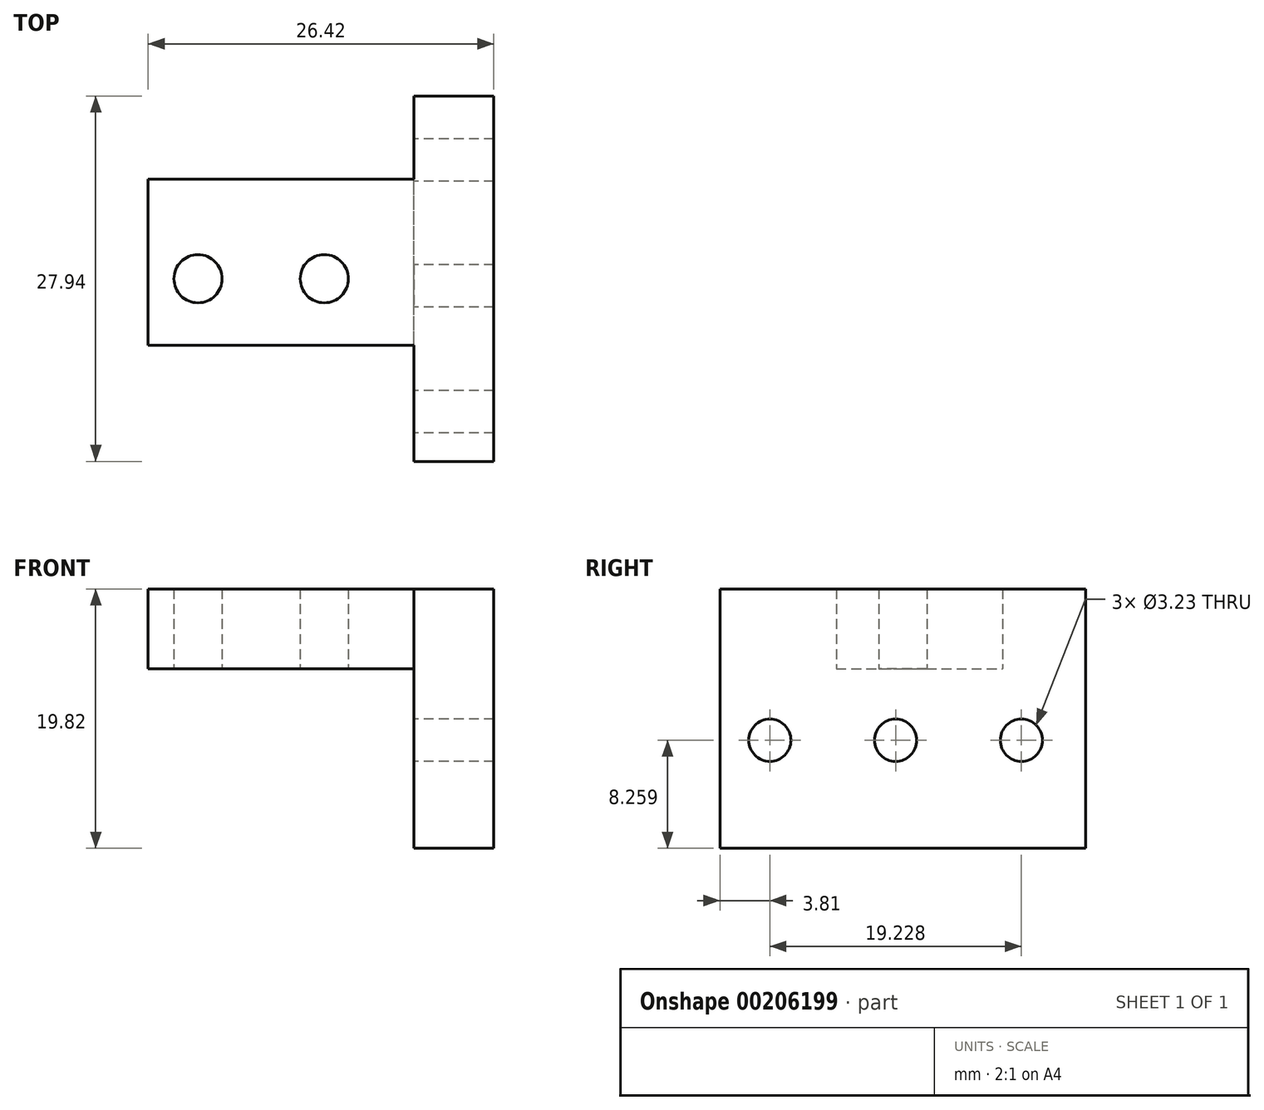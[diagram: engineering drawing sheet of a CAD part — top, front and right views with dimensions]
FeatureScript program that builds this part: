
annotation { "Feature Type Name" : "Feature", "Feature Type Description" : "" }
export const myFeature = defineFeature(function(context is Context, id is Id, definition is map)
    precondition{}
    {
        {
            var Q0;
            Q0=qCreatedBy(makeId("Top.planeOp"),FACE);
            var sketch = newSketch(context, id + "F0", { "sketchPlane" : qUnion([Q0])});
            skLineSegment(sketch, "E0.bottom", {"start": v(0, 0) * mm, "end": v(20.32, 0) * mm});
            skLineSegment(sketch, "E0.top", {"start": v(0, 12.7) * mm, "end": v(20.32, 12.7) * mm});
            skLineSegment(sketch, "E0.left", {"start": v(0, 0) * mm, "end": v(0, 12.7) * mm});
            skLineSegment(sketch, "E0.right", {"start": v(20.32, 0) * mm, "end": v(20.32, 12.7) * mm});
            skCircle(sketch, "E1", {"center": v(3.8, 5.08) * mm, "radius": 1.84 * mm});
            skCircle(sketch, "E2.1.0.0", {"center": v(13.46, 5.08) * mm, "radius": 1.84 * mm});
            skLineSegment(sketch, "E2.direction1", {"start": v(3.8, 5.08) * mm, "end": v(13.46, 5.08) * mm, "construction": true});
            skSolve(sketch);
        }
        {
            var Q0;
            Q0 = qSketchRegion(id + "F0", true);
            extrude(context, id + "F1", {"entities" : qUnion([Q0]), "depth" : 6.1 * mm});
        }
        {
            var Q0;
            Q0=makeQuery(id+"F1.opExtrude","CAP_FACE",FACE,{"disambiguationData":[OSD([sQuery(id+"F0.wireOp",EDGE,"E0.bottom"),sQuery(id+"F0.wireOp",EDGE,"E0.top"),sQuery(id+"F0.wireOp",EDGE,"E0.left"),sQuery(id+"F0.wireOp",EDGE,"E0.right"),sQuery(id+"F0.wireOp",EDGE,"E1"),sQuery(id+"F0.wireOp",EDGE,"E2.1.0.0")])],"isStart":false});
            var sketch = newSketch(context, id + "F2", { "sketchPlane" : qUnion([Q0])});
            skLineSegment(sketch, "E3.bottom", {"start": v(26.42, -8.9) * mm, "end": v(20.32, -8.9) * mm});
            skLineSegment(sketch, "E3.top", {"start": v(20.32, 19.05) * mm, "end": v(26.42, 19.05) * mm});
            skLineSegment(sketch, "E3.right", {"start": v(20.32, -8.9) * mm, "end": v(20.32, 19.05) * mm});
            skLineSegment(sketch, "E4", {"start": v(26.42, 19.05) * mm, "end": v(26.42, -8.9) * mm});
            skSolve(sketch);
        }
        {
            var Q0;
            Q0 = qSketchRegion(id + "F2", true);
            extrude(context, id + "F3", {"entities" : qUnion([Q0]), "operationType" : NewBodyOperationType.ADD, "oppositeDirection" : true, "depth" : 19.8 * mm});
        }
        {
            var Q0;
            Q0=makeQuery(id+"F3.opExtrude","SWEPT_FACE",FACE,{"disambiguationData":[OSD([sQuery(id+"F2.wireOp",EDGE,"E3.right")])]});
            var sketch = newSketch(context, id + "F4", { "sketchPlane" : qUnion([Q0])});
            skCircle(sketch, "E5", {"center": v(5.08, -5.46) * mm, "radius": 1.61 * mm});
            skCircle(sketch, "E6.1.0.0", {"center": v(-4.53, -5.46) * mm, "radius": 1.61 * mm});
            skCircle(sketch, "E6.2.0.0", {"center": v(-14.15, -5.46) * mm, "radius": 1.61 * mm});
            skLineSegment(sketch, "E6.direction1", {"start": v(5.08, -5.46) * mm, "end": v(-4.53, -5.46) * mm, "construction": true});
            skSolve(sketch);
        }
        {
            var Q0;
            Q0 = qSketchRegion(id + "F4", true);
            extrude(context, id + "F5", {"entities" : qUnion([Q0]), "operationType" : NewBodyOperationType.REMOVE, "oppositeDirection" : true, "depth" : 25.4 * mm});
        }
    });
